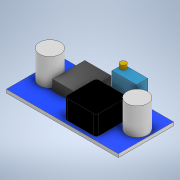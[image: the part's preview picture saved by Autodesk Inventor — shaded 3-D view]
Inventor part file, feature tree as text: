
AUTODESK INVENTOR PART (.ipt)
format: ipt  version: 2022 (Build 260153000, 153)  size: 188,928 bytes
history: native  units: in
note: dims shown in document units (in); Inventor stores cm internally (conversion verified against a paired STEP export)
features: extrude x6, sketch x6
ambient origin geometry x8: Origin, YZ Plane, XZ Plane, XY Plane, X Axis, Y Axis, Z Axis, Center Point
bodies: Solid1 (feature_tree)
feature tree (12):
  extrude  "Extrusion1"  Depth=0.8346in
  extrude  "Extrusion2"  Depth=0.8465in
  extrude  "Extrusion3"  Depth=0.4882in
  extrude  "Extrusion4"  Depth=0.3228in
  extrude  "Extrusion5"  Depth=0.1575in TaperAngle=0.0deg
  extrude  "Extrusion6"  Depth=0.4803in
  sketch  "Sketch1"  dims[d0=1.6929in d1=0.8346in]
  sketch  "Sketch2"  dims[d2=0.4173in d3=0.8465in]
  sketch  "Sketch3"  dims[d4=0.0516in d5=0.0in d6=0.4882in]
  sketch  "Sketch4"  dims[d7=0.3996in d8=0.3228in]
  sketch  "Sketch5"  dims[d9=0.374in d10=0.1575in d11=0.0in]
  sketch  "Sketch6"  dims[d12=0.4803in d13=0.4803in d14=0.0472in d15=0.3819in d16=0.0394in d17=0.2913in d18=0.0in d19=0.1697in d20=0.3728in d21=0.3689in d22=0.0197in d23=0.3937in d24=0.0in d25=0.0886in d26=0.0472in d27=0.0472in d28=0.0634in d29=0.0in d30=0.315in d31=0.315in d32=0.4657in d33=0.1799in d34=0.2055in d35=0.4516in d36=0.4134in d37=0.0in]
